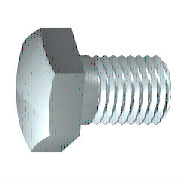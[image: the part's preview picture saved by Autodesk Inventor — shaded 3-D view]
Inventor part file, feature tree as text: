
AUTODESK INVENTOR PART (.ipt)
format: ipt  version: 2020 (Build 240168000, 168)  size: 193,024 bytes
history: native  units: mm (DEFAULTED — no unit token found)
features: sketch x3, extrude x1, chamfer x1, plane x1
ambient origin geometry x7: Origin, YZ Plane, XZ Plane, X Axis, Y Axis, Z Axis, Center Point
bodies: Solid1 (feature_tree), Body (feature_tree)
feature tree (6):
  extrude  "Head"  Depth=47.9mm
  chamfer  "Chamfer1"  Distance=2.4mm
  plane  "Work Plane1"
  sketch  "Sketch1"  dims[d0=50.0mm d1=47.9mm]
  sketch  "Sketch2"  dims[d2=4.0mm]
  sketch  "Sketch4"  dims[d12=90.0deg d3=2.4mm d4=0.0mm d5=30.0deg d21=90.0deg d6=0.429415mm d7=0.429515mm d8=0.0mm d9=0.4001mm d10=5.9mm d11=7.0mm d13=0.429515mm d14=3.621114mm d15=47.9mm d16=0.0mm d19=7.0mm d55=45.0deg d57=0.0mm d58=0.0mm]
